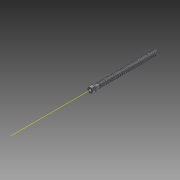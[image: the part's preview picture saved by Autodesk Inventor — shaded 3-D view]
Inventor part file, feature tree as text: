
AUTODESK INVENTOR PART (.ipt)
format: ipt  version: 2012 (Build 160160000, 160)  size: 1,796,608 bytes
history: native  units: in
note: dims shown in document units (in); Inventor stores cm internally (conversion verified against a paired STEP export)
features: sketch x15, extrude x14, plane x10, fillet x5, projected_geometry x2, helix x1, chamfer x1, other x1
ambient origin geometry x8: Origin, YZ Plane, XZ Plane, XY Plane, X Axis, Y Axis, Z Axis, Center Point
feature tree (49):
  plane  "Work Plane2"
  plane  "Work Plane5"
  plane  "Work Plane6"
  extrude  "Extrusion2"  Depth=0.3937in TaperAngle=0.0deg
  sketch  "Sketch9"  dims[d33=6.674in d34=0.0in d37=0.1969in]
  plane  "Work Plane7"
  extrude  "Extrusion7"  Depth=0.1969in
  plane  "Work Plane10"
  sketch  "Sketch10"  dims[d56=0.5512in d57=0.3937in d58=0.0in]
  sketch  "Sketch11"  dims[d60=0.1181in d61=0.2362in]
  plane  "Work Plane8"
  extrude  "Extrusion9"  Depth=0.3937in TaperAngle=0.0deg
  plane  "Work Plane9"
  plane  "Work Plane11"
  extrude  "Extrusion10"  Depth=0.2362in
  extrude  "Extrusion13"  Depth=0.3937in
  fillet  "Fillet10"  Radius=0.1181in
  helix  "Coil2"  [1 undecoded]
  chamfer  "Chamfer1"  Distance=0.1181in
  plane  "Work Plane12"
  extrude  "Extrusion12"  Depth=0.0787in
  fillet  "Fillet7"  Radius=0.0118in
  extrude  "Extrusion16"  Depth=0.4134in TaperAngle=0.0deg
  extrude  "Extrusion17"  Depth=0.0118in TaperAngle=0.0deg
  extrude  "Extrusion18"  Depth=0.0394in
  extrude  "Extrusion19"  Depth=0.0059in
  fillet  "Fillet17"  Radius=0.3937in
  fillet  "Fillet18"  Radius=0.2756in
  extrude  "Extrusion20"  Depth=0.3937in TaperAngle=0.0deg
  extrude  "Extrusion21"  Depth=0.3937in TaperAngle=0.0deg
  plane  "Work Plane14"
  extrude  "Extrusion23"  [1 undecoded]
  fillet  "Fillet19"  [1 undecoded]
  extrude  "Extrusion24"  [1 undecoded]
  other  "Work Axis1"
  sketch  "Sketch4"  dims[d5=0.5in d6=0.0in d27=0.3937in d28=0.0in]
  projected_geometry  "Projected Loop3"
  sketch  "Sketch14"  dims[d62=0.3937in d63=11.0236in d64=0.0in d65=90.0deg d66=90.0deg d67=0.0in d68=0.0in d75=0.3937in d76=0.1181in d77=0.1181in d78=0.0in]
  sketch  "Sketch16"  dims[d79=0.0197in]
  sketch  "Sketch17"  dims[d81=0.6398in d82=0.1181in d83=0.0in]
  sketch  "Sketch25"  dims[d89=0.0787in d96=0.0787in d97=0.0492in d98=0.481in d103=0.0118in d104=0.0in]
  sketch  "Sketch26"  dims[d105=0.0118in d106=0.0in d107=0.4134in d108=0.0in]
  projected_geometry  "Projected Loop11"
  sketch  "Sketch27"  dims[d109=0.0118in d110=0.0in d111=0.0118in d112=0.0in]
  sketch  "Sketch28"  dims[d113=0.0787in d114=0.0394in]
  sketch  "Sketch29"  dims[d115=0.0394in d116=0.0059in d117=0.3937in d118=0.0in d119=0.2756in]
  sketch  "Sketch30"  dims[d120=0.1969in d121=0.0in d124=0.3937in d125=0.0in]
  sketch  "Sketch32"  dims[d126=0.0394in d127=0.3937in d128=0.0in]
  sketch  "Sketch33"
note: 4 required parameter values undecoded (feature->parameter linkage not recoverable at this tier; creation-order binding heuristic only, values carry confidence <= 0.55)
